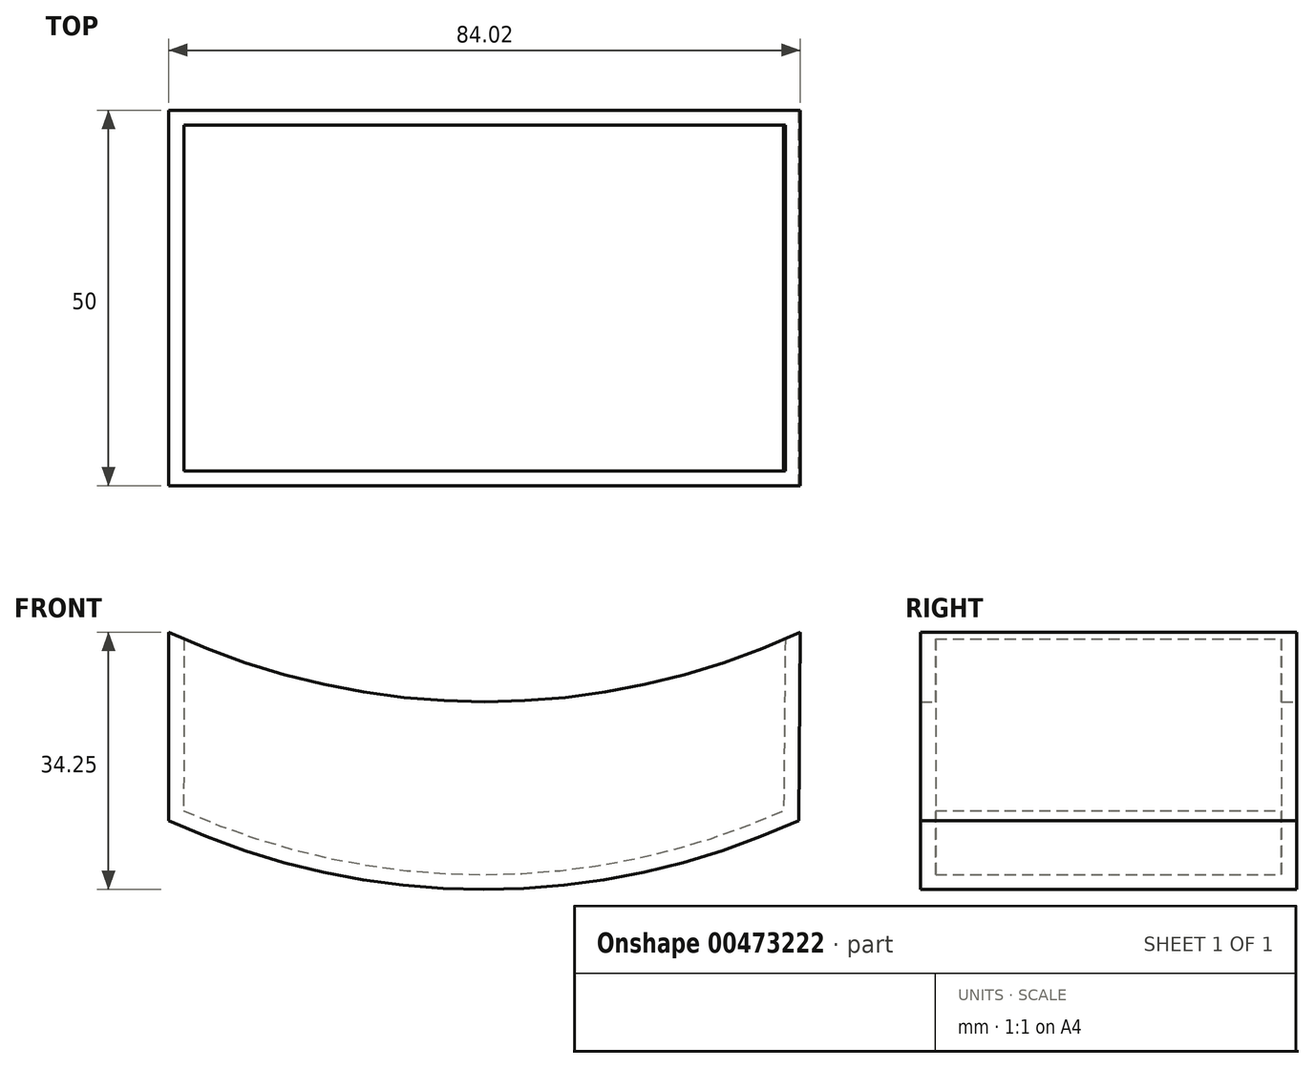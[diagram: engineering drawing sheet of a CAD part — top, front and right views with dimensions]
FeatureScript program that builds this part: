
annotation { "Feature Type Name" : "Feature", "Feature Type Description" : "" }
export const myFeature = defineFeature(function(context is Context, id is Id, definition is map)
    precondition{}
    {
        {
            var Q0;
            Q0=qCreatedBy(makeId("Front.planeOp"),FACE);
            var sketch = newSketch(context, id + "F0", { "sketchPlane" : qUnion([Q0])});
            skPoint(sketch, "E0", {"position": v(-42, 0) * mm});
            skPoint(sketch, "E1", {"position": v(0, 0) * mm});
            skPoint(sketch, "E2", {"position": v(42, 0) * mm});
            skArc(sketch, "E3", {"start": v(-42, 0) * mm, "mid": v(0, -9.25) * mm, "end": v(42, 0) * mm});
            skPoint(sketch, "E4", {"position": v(-42.02, -25.05) * mm});
            skPoint(sketch, "E5", {"position": v(41.77, -25.05) * mm});
            skArc(sketch, "E6", {"start": v(-42.02, -25.05) * mm, "mid": v(-0.12, -34.25) * mm, "end": v(41.77, -25.05) * mm});
            skLineSegment(sketch, "E7", {"start": v(-42, 0) * mm, "end": v(-42.02, -25.05) * mm});
            skLineSegment(sketch, "E8", {"start": v(42, 0) * mm, "end": v(41.77, -25.05) * mm});
            skSolve(sketch);
        }
        {
            var Q0;
            Q0 = qSketchRegion(id + "F0", true);
            extrude(context, id + "F1", {"entities" : qUnion([Q0]), "depth" : 50 * mm});
        }
        {
            var Q0;
            Q0=makeQuery(id+"F1.opExtrude","SWEPT_FACE",FACE,{"disambiguationData":[OSD([sQuery(id+"F0.wireOp",EDGE,"E3")])]});
            shell(context, id + "F2", {"entities" : qUnion([Q0]), "thickness" : 2 * mm});
        }
    });
